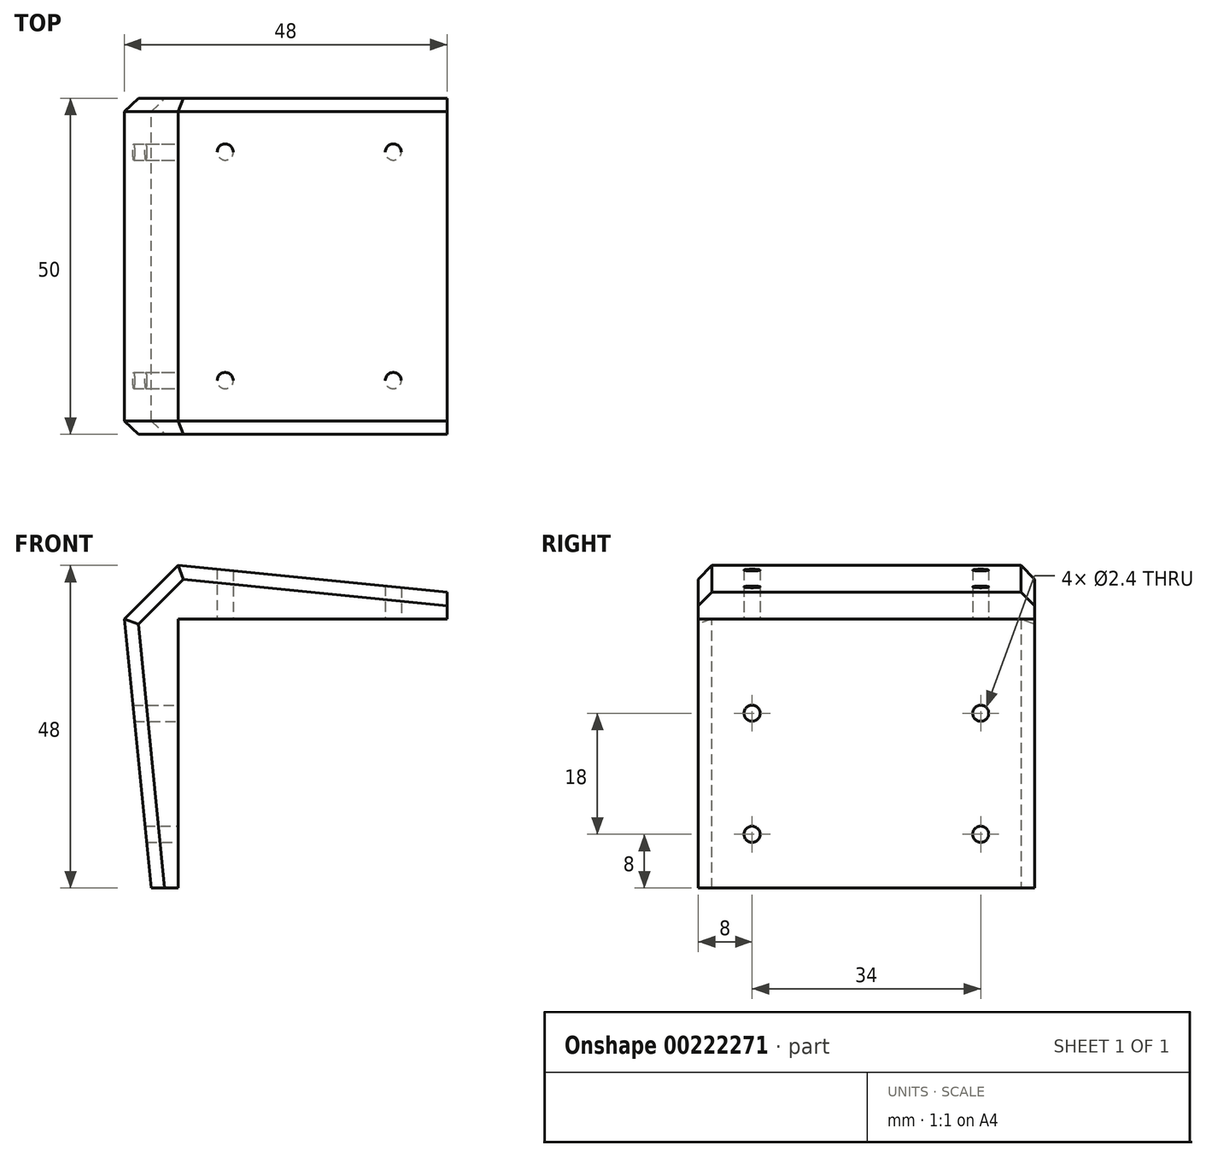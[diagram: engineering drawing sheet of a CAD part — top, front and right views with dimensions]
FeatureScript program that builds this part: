
annotation { "Feature Type Name" : "Feature", "Feature Type Description" : "" }
export const myFeature = defineFeature(function(context is Context, id is Id, definition is map)
    precondition{}
    {
        {
            var Q0;
            Q0=qCreatedBy(makeId("Front.planeOp"),FACE);
            var sketch = newSketch(context, id + "F0", { "sketchPlane" : qUnion([Q0])});
            skLineSegment(sketch, "E0", {"start": v(0, 0) * mm, "end": v(0, -40) * mm});
            skLineSegment(sketch, "E1", {"start": v(0, -40) * mm, "end": v(-4, -40) * mm});
            skLineSegment(sketch, "E2", {"start": v(-4, -40) * mm, "end": v(-8, 0) * mm});
            skLineSegment(sketch, "E3", {"start": v(-8, 0) * mm, "end": v(0, 8) * mm});
            skLineSegment(sketch, "E4", {"start": v(0, 8) * mm, "end": v(40, 4) * mm});
            skLineSegment(sketch, "E5", {"start": v(40, 4) * mm, "end": v(40, 0) * mm});
            skLineSegment(sketch, "E6", {"start": v(40, 0) * mm, "end": v(0, 0) * mm});
            skSolve(sketch);
        }
        {
            var Q0;
            Q0=makeQuery(id+"F0.imprint","IMPRINT",FACE,{"disambiguationData":[TD([[makeQuery(id+"F0.imprint","IMPRINT",EDGE,{"derivedFrom":sQuery(id+"F0.wireOp",EDGE,"E0")}),-1.0]])]});
            extrude(context, id + "F1", {"entities" : qUnion([Q0]), "depth" : 50 * mm});
        }
        {
            var Q0;
            Q0=makeQuery(id+"F1.opExtrude","SWEPT_FACE",FACE,{"disambiguationData":[OSD([sQuery(id+"F0.wireOp",EDGE,"E6")])]});
            var sketch = newSketch(context, id + "F2", { "sketchPlane" : qUnion([Q0])});
            skPoint(sketch, "E7", {"position": v(7, 42) * mm});
            skPoint(sketch, "E8", {"position": v(32, 42) * mm});
            skPoint(sketch, "E9", {"position": v(32, 8) * mm});
            skPoint(sketch, "E10", {"position": v(7, 8) * mm});
            skSolve(sketch);
        }
        {
            var Q0;
            Q0=sQuery(id+"F2.wireOp",VERTEX,"E8");
            var Q1;
            Q1=sQuery(id+"F2.wireOp",VERTEX,"E9");
            var Q2;
            Q2=sQuery(id+"F2.wireOp",VERTEX,"E10");
            var Q3;
            Q3=sQuery(id+"F2.wireOp",VERTEX,"E7");
            var Q4;
            Q4=makeQuery(id+"F1.opExtrude","SWEPT_BODY",BODY,{"disambiguationData":[OSD([sQuery(id+"F0.wireOp",EDGE,"E0"),sQuery(id+"F0.wireOp",EDGE,"E1"),sQuery(id+"F0.wireOp",EDGE,"E2"),sQuery(id+"F0.wireOp",EDGE,"E3"),sQuery(id+"F0.wireOp",EDGE,"E4"),sQuery(id+"F0.wireOp",EDGE,"E5"),sQuery(id+"F0.wireOp",EDGE,"E6")])]});
            hole(context, id + "F3", {"style" : HoleStyle.SIMPLE, "endStyle" : HoleEndStyle.THROUGH, "standardTappedOrClearance" : lookupTablePath({ "standard" : "ISO", "engagement" : "75%", "pitch" : "0.6 mm", "size" : "M3", "type" : "Tapped" }), "standardBlindInLast" : lookupTablePath({ "standard" : "ISO", "engagement" : "75%", "pitch" : "0.6 mm", "size" : "M3", "type" : "Tapped" }), "holeDiameter" : 2.4 * mm, "locations" : qUnion([Q0, Q1, Q2, Q3]), "scope" : qUnion([Q4]), "isTappedThrough" : true, "showTappedDepth" : true});
        }
        {
            var Q0;
            Q0=makeQuery(id+"F1.opExtrude","SWEPT_FACE",FACE,{"disambiguationData":[OSD([sQuery(id+"F0.wireOp",EDGE,"E0")])]});
            var sketch = newSketch(context, id + "F4", { "sketchPlane" : qUnion([Q0])});
            skPoint(sketch, "E11", {"position": v(-42, -32) * mm});
            skPoint(sketch, "E12", {"position": v(-8, -14) * mm});
            skPoint(sketch, "E13", {"position": v(-8, -32) * mm});
            skPoint(sketch, "E14", {"position": v(-42, -14) * mm});
            skSolve(sketch);
        }
        {
            var Q0;
            Q0=sQuery(id+"F4.wireOp",VERTEX,"E11");
            var Q1;
            Q1=sQuery(id+"F4.wireOp",VERTEX,"E14");
            var Q2;
            Q2=sQuery(id+"F4.wireOp",VERTEX,"E13");
            var Q3;
            Q3=sQuery(id+"F4.wireOp",VERTEX,"E12");
            var Q4;
            Q4=makeQuery(id+"F1.opExtrude","SWEPT_BODY",BODY,{"disambiguationData":[OSD([sQuery(id+"F0.wireOp",EDGE,"E0"),sQuery(id+"F0.wireOp",EDGE,"E1"),sQuery(id+"F0.wireOp",EDGE,"E2"),sQuery(id+"F0.wireOp",EDGE,"E3"),sQuery(id+"F0.wireOp",EDGE,"E4"),sQuery(id+"F0.wireOp",EDGE,"E5"),sQuery(id+"F0.wireOp",EDGE,"E6")])]});
            hole(context, id + "F5", {"style" : HoleStyle.SIMPLE, "endStyle" : HoleEndStyle.THROUGH, "standardTappedOrClearance" : lookupTablePath({ "standard" : "ISO", "engagement" : "75%", "pitch" : "0.6 mm", "size" : "M3", "type" : "Tapped" }), "standardBlindInLast" : lookupTablePath({ "standard" : "ISO", "engagement" : "75%", "pitch" : "0.6 mm", "size" : "M3", "type" : "Tapped" }), "holeDiameter" : 2.4 * mm, "locations" : qUnion([Q0, Q1, Q2, Q3]), "scope" : qUnion([Q4]), "isTappedThrough" : true, "showTappedDepth" : true});
        }
        {
            var Q0;
            Q0=makeQuery(id+"F1.opExtrude","CAP_EDGE",EDGE,{"disambiguationData":[OSD([sQuery(id+"F0.wireOp",EDGE,"E4")])],"isStart":false});
            var Q1;
            Q1=makeQuery(id+"F1.opExtrude","CAP_EDGE",EDGE,{"disambiguationData":[OSD([sQuery(id+"F0.wireOp",EDGE,"E3")])],"isStart":false});
            var Q2;
            Q2=makeQuery(id+"F1.opExtrude","CAP_EDGE",EDGE,{"disambiguationData":[OSD([sQuery(id+"F0.wireOp",EDGE,"E2")])],"isStart":false});
            var Q3;
            Q3=makeQuery(id+"F1.opExtrude","CAP_EDGE",EDGE,{"disambiguationData":[OSD([sQuery(id+"F0.wireOp",EDGE,"E2")])],"isStart":true});
            var Q4;
            Q4=makeQuery(id+"F1.opExtrude","CAP_EDGE",EDGE,{"disambiguationData":[OSD([sQuery(id+"F0.wireOp",EDGE,"E4")])],"isStart":true});
            var Q5;
            Q5=makeQuery(id+"F1.opExtrude","CAP_EDGE",EDGE,{"disambiguationData":[OSD([sQuery(id+"F0.wireOp",EDGE,"E3")])],"isStart":true});
            chamfer(context, id + "F6", {"entities" : qUnion([Q0, Q1, Q2, Q3, Q4, Q5]), "width" : 2 * mm, "tangentPropagation" : true});
        }
    });
